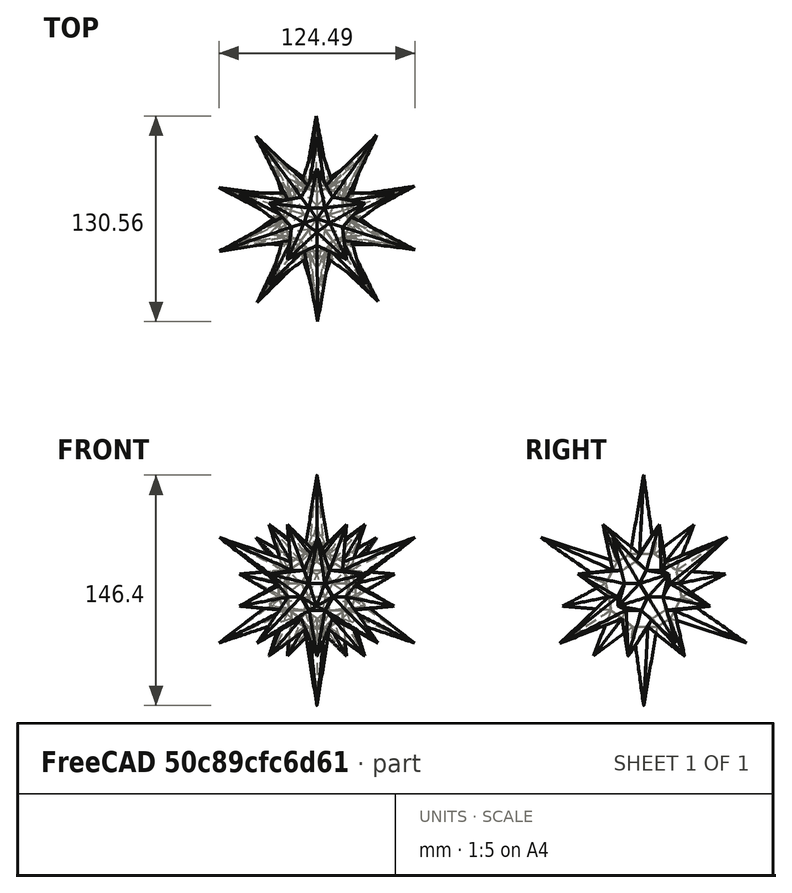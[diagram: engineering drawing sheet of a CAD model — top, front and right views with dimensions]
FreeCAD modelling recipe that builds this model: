
FCSTD DOCUMENT  (FreeCAD 0.18R13516 (Git))
Label: ESTRELA
License: All rights reserved
LicenseURL: http://en.wikipedia.org/wiki/All_rights_reserved
objects: Part::FeaturePython×9, Part::RegularPolygon×2, Part::Vertex×2, Part::Loft×2, Part::Compound×1
note: 16 computed .brp shape members not serialized (recipe doc carries the construction recipe); baked Part::Feature solids carry a one-line shape summary decoded from their .brp

FEATURE [Part::RegularPolygon] RegularPolygon  label="Regular polygon"
  AttacherType = Attacher::AttachEngine3D
  Circumradius = 8.5
  Polygon = 5
FEATURE [Part::RegularPolygon] RegularPolygon001  label="Regular polygon001"
  AttacherType = Attacher::AttachEngine3D
  Circumradius = 10
  Polygon = 6
FEATURE [Part::Vertex] Vertex
  AttacherType = Attacher::AttachEngine3D
  X = 0
  Y = 0
  Z = 50
FEATURE [Part::Vertex] Vertex001
  AttacherType = Attacher::AttachEngine3D
  X = 0
  Y = 0
  Z = 30
FEATURE [Part::Loft] Loft
  Closed = false
  MaxDegree = 5
  Placement = pos=(-0.0032056,0.00441297,46.4009) rot=(1.1e-05,1.1e-05,1;4.7123rad)
  Ruled = true
  Sections = -> [RegularPolygon,Vertex]
  Solid = true
FEATURE [Part::Loft] Loft001
  Closed = false
  MaxDegree = 5
  Placement = pos=(-8.08863,-11.1349,41.1424) rot=(0.242954,0.218735,-0.945055;2.74515rad)
  Ruled = true
  Sections = -> [RegularPolygon001,Vertex001]
  Solid = true
FEATURE [Part::FeaturePython] bola_01  # a2plus imported part (geometry in sourceFile) (typed FeaturePython)
  fixedPosition = true
  sourceFile = <userpath>/WORK/FREECAD/50- BOLA/bola.fcstd
  timeLastImport = 1.54371e+09
  updateColors = true
FEATURE [Part::FeaturePython] Clone  label="Loft002"  # Draft clone (typed FeaturePython)
  AttacherType = Attacher::AttachEngine3D
  Fuse = false
  Objects = -> [Loft001]
  Placement = pos=(-13.1776,-18.128,27.409) rot=(0.200927,0.618389,-0.759753;3.62563rad)
  Scale = (1,1,1)
FEATURE [Part::FeaturePython] Clone001  label="Loft003"  # Draft clone (typed FeaturePython)
  AttacherType = Attacher::AttachEngine3D
  Fuse = false
  Objects = -> [Loft]
  Placement = pos=(-12.2819,-16.928,12.7647) rot=(0.705224,-0.701916,0.099867;2.06686rad)
  Scale = (1,1,1)
FEATURE [Part::FeaturePython] Clone002  label="Loft004"  # Draft clone (typed FeaturePython)
  AttacherType = Attacher::AttachEngine3D
  Fuse = false
  Objects = -> [Clone]
  Placement = pos=(-13.1008,-4.2557,5.25562) rot=(0.79384,-0.576133,-0.194649;2.61714rad)
  Scale = (1,1,1)
FEATURE [Part::FeaturePython] Clone003  label="Loft005"  # Draft clone (typed FeaturePython)
  AttacherType = Attacher::AttachEngine3D
  Fuse = false
  Objects = -> [Clone001]
  Placement = pos=(-0.0025866,-0.00486265,-0.000794627) rot=(-0.987688,-0.156434,0;3.14159rad)
  Scale = (1,1,1)
FEATURE [Part::FeaturePython] Clone004  label="Loft006"  # Draft clone (typed FeaturePython)
  AttacherType = Attacher::AttachEngine3D
  Fuse = false
  Objects = -> [Loft]
  Placement = pos=(-0.00125621,-20.9324,33.6014) rot=(-0.712073,-0.370339,0.596491;4.87678rad)
  Scale = (1,1,1)
FEATURE [Part::FeaturePython] Clone005  label="Loft007"  # Draft clone (typed FeaturePython)
  AttacherType = Attacher::AttachEngine3D
  Fuse = false
  Objects = -> [Clone]
  Placement = pos=(0.0206678,-22.2864,19.0126) rot=(0.004878,0.773202,-0.634141;3.1498rad)
  Scale = (1,1,1)
FEATURE [Part::FeaturePython] Clone006  label="Loft008"  # Draft clone (typed FeaturePython)
  AttacherType = Attacher::AttachEngine3D
  Fuse = false
  Objects = -> [Clone005]
  Placement = pos=(-0.00169361,-13.7746,5.25639) rot=(-0.000508,0.947342,-0.320224;3.14118rad)
  Scale = (1,1,1)
FEATURE [Part::Compound] Compound
  Links = -> [Clone006,Clone005,Clone004,Clone003,Clone002,Clone001,Clone,Loft001,Loft]
FEATURE [Part::FeaturePython] Array  # Draft array (typed FeaturePython)
  Angle = 360
  ArrayType = 1
  Axis = (0,0,1)
  Base = -> Compound
  Center = (0,0,0)
  Fuse = false
  IntervalAxis = (0,0,0)
  IntervalX = (1,0,0)
  IntervalY = (0,1,0)
  IntervalZ = (0,0,0)
  NumberPolar = 5
  NumberX = 2
  NumberY = 2
  NumberZ = 1
